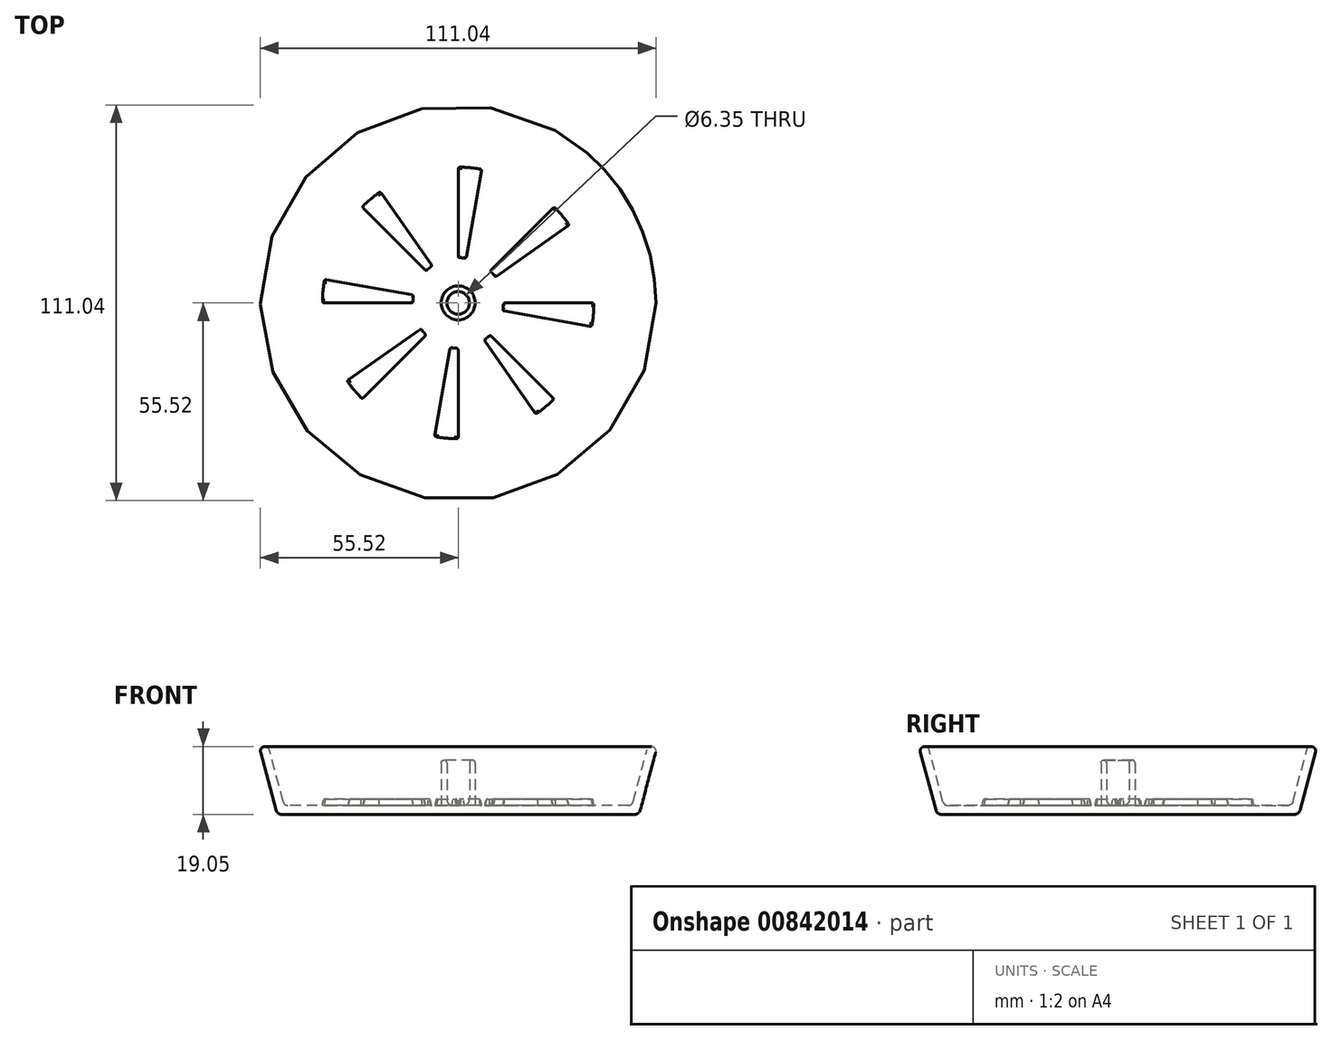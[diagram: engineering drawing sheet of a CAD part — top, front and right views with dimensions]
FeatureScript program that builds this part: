
annotation { "Feature Type Name" : "Feature", "Feature Type Description" : "" }
export const myFeature = defineFeature(function(context is Context, id is Id, definition is map)
    precondition{}
    {
        {
            var Q0;
            Q0=qCreatedBy(makeId("Top.planeOp"),FACE);
            var sketch = newSketch(context, id + "F0", { "sketchPlane" : qUnion([Q0])});
            skCircle(sketch, "E0.cCircle", {"center": v(0, 0) * mm, "radius": 38.1 * mm, "construction": true});
            skLineSegment(sketch, "E0.0", {"start": v(1.85, 47.06) * mm, "end": v(45.33, 12.78) * mm, "construction": true});
            skLineSegment(sketch, "E0.1", {"start": v(45.33, 12.78) * mm, "end": v(26.16, -39.16) * mm, "construction": true});
            skLineSegment(sketch, "E0.2", {"start": v(26.16, -39.16) * mm, "end": v(-29.16, -36.98) * mm, "construction": true});
            skLineSegment(sketch, "E0.3", {"start": v(-29.16, -36.98) * mm, "end": v(-44.18, 16.3) * mm, "construction": true});
            skLineSegment(sketch, "E0.4", {"start": v(-44.18, 16.3) * mm, "end": v(1.85, 47.06) * mm, "construction": true});
            skPoint(sketch, "E0.0.midPoint", {"position": v(23.59, 29.92) * mm});
            skCircle(sketch, "E1", {"center": v(0, 0) * mm, "radius": 50.8 * mm});
            skSolve(sketch);
        }
        {
            var Q0;
            Q0 = qSketchRegion(id + "F0", true);
            extrude(context, id + "F1", {"entities" : qUnion([Q0]), "depth" : 19.05 * mm, "offsetDistance" : 25.4 * mm, "hasDraft" : true, "draftAngle" : 15 * degree});
        }
        {
            var Q0;
            Q0=makeQuery(id+"F1.opExtrude","CAP_FACE",FACE,{"disambiguationData":[OSD([sQuery(id+"F0.wireOp",EDGE,"E1")])],"isStart":false});
            shell(context, id + "F2", {"entities" : qUnion([Q0]), "thickness" : 2.54 * mm});
        }
        {
            var Q0;
            Q0=makeQuery(id+"F1.opExtrude","CAP_FACE",FACE,{"disambiguationData":[OSD([sQuery(id+"F0.wireOp",EDGE,"E1")])],"isStart":false});
            var Q1;
            {var subQ0=sQuery(id+"F0.wireOp",EDGE,"E1");Q1=makeQuery(id+"F2.opShell","OFFSET_EDGE",EDGE,{"disambiguationData":[OSD([subQ0]),TDD([makeQuery(id+"F1.opExtrude","CAP_EDGE",EDGE,{"disambiguationData":[OSD([subQ0])],"isStart":true})])]});}
            fillet(context, id + "F3", {"entities" : qUnion([Q0, Q1]), "radius" : 1.27 * mm, "tangentPropagation" : true, "allowEdgeOverflow" : false});
        }
        {
            var Q0;
            {var subQ0=sQuery(id+"F0.wireOp",EDGE,"E1");Q0=makeQuery(id+"F2.opShell","OFFSET_FACE",FACE,{"disambiguationData":[OSD([subQ0]),TDD([makeQuery(id+"F1.opExtrude","CAP_FACE",FACE,{"disambiguationData":[OSD([subQ0])],"isStart":true})])]});}
            var sketch = newSketch(context, id + "F4", { "sketchPlane" : qUnion([Q0])});
            skCircle(sketch, "E2", {"center": v(0, 0) * mm, "radius": 4.76 * mm});
            skCircle(sketch, "E3", {"center": v(0, 0) * mm, "radius": 3.18 * mm});
            skSolve(sketch);
        }
        {
            var Q0;
            Q0=makeQuery(id+"F4.imprint","IMPRINT",FACE,{"disambiguationData":[TD([[makeQuery(id+"F4.imprint","IMPRINT",EDGE,{"derivedFrom":sQuery(id+"F4.wireOp",EDGE,"E2")}),1.0]])]});
            extrude(context, id + "F5", {"entities" : qUnion([Q0]), "operationType" : NewBodyOperationType.ADD, "depth" : 12.7 * mm, "offsetDistance" : 25.4 * mm});
        }
        {
            var Q0;
            Q0=makeQuery(id+"F1.opExtrude","CAP_FACE",FACE,{"disambiguationData":[OSD([sQuery(id+"F0.wireOp",EDGE,"E1")])],"isStart":true});
            var Q1;
            Q1=makeQuery(id+"F5.opExtrude","CAP_EDGE",EDGE,{"disambiguationData":[OSD([sQuery(id+"F4.wireOp",EDGE,"E2")])],"isStart":true});
            fillet(context, id + "F6", {"entities" : qUnion([Q0, Q1]), "radius" : 1.59 * mm, "tangentPropagation" : true, "allowEdgeOverflow" : false});
        }
        {
            var Q0;
            Q0=makeQuery(id+"F5.opExtrude","CAP_EDGE",EDGE,{"disambiguationData":[OSD([sQuery(id+"F4.wireOp",EDGE,"E3")])],"isStart":true});
            fillet(context, id + "F7", {"entities" : qUnion([Q0]), "radius" : 1.59 * mm, "tangentPropagation" : true, "allowEdgeOverflow" : false});
        }
        {
            var Q0;
            Q0=makeQuery(id+"F5.opExtrude","CAP_FACE",FACE,{"disambiguationData":[OSD([sQuery(id+"F4.wireOp",EDGE,"E2"),sQuery(id+"F4.wireOp",EDGE,"E3")])],"isStart":false});
            fillet(context, id + "F8", {"entities" : qUnion([Q0]), "radius" : 0.76 * mm, "tangentPropagation" : true, "allowEdgeOverflow" : false});
        }
        {
            var Q0;
            {var subQ0=sQuery(id+"F0.wireOp",EDGE,"E1");Q0=makeQuery(id+"F5.boolean.opBoolean","SPLIT",FACE,{"disambiguationData":[TD([makeQuery(id+"F5.opExtrude","SWEPT_FACE",FACE,{"disambiguationData":[OSD([sQuery(id+"F4.wireOp",EDGE,"E2")])]})])],"derivedFrom":makeQuery(id+"F2.opShell","OFFSET_FACE",FACE,{"disambiguationData":[OSD([subQ0]),TDD([makeQuery(id+"F1.opExtrude","CAP_FACE",FACE,{"disambiguationData":[OSD([subQ0])],"isStart":true})])]})});}
            var sketch = newSketch(context, id + "F9", { "sketchPlane" : qUnion([Q0])});
            skArc(sketch, "E4", {"start": v(2.2, 12.5) * mm, "mid": v(1.1, 12.65) * mm, "end": v(0, 12.7) * mm});
            skArc(sketch, "E5.0", {"start": v(6.62, 37.52) * mm, "mid": v(3.32, 37.96) * mm, "end": v(0, 38.1) * mm});
            skLineSegment(sketch, "E6", {"start": v(0, 38.1) * mm, "end": v(0, 12.7) * mm});
            skLineSegment(sketch, "E7.1.0", {"start": v(6.62, 37.52) * mm, "end": v(2.2, 12.5) * mm});
            skLineSegment(sketch, "E7.anchor1", {"start": v(0, 0) * mm, "end": v(0, 12.7) * mm, "construction": true});
            skLineSegment(sketch, "E7.anchor2", {"start": v(0, 0) * mm, "end": v(2.2, 12.5) * mm, "construction": true});
            skSolve(sketch);
        }
        {
            var Q0;
            Q0 = qSketchRegion(id + "F9", true);
            extrude(context, id + "F10", {"entities" : qUnion([Q0]), "operationType" : NewBodyOperationType.ADD, "depth" : 1.78 * mm, "offsetDistance" : 25.4 * mm, "hasDraft" : true, "draftAngle" : 10 * degree, "draftPullDirection" : true});
        }
        {
            var Q0;
            Q0=makeQuery(id+"F10.opExtrude","CAP_FACE",FACE,{"disambiguationData":[OSD([sQuery(id+"F9.wireOp",EDGE,"E4"),sQuery(id+"F9.wireOp",EDGE,"E5.0"),sQuery(id+"F9.wireOp",EDGE,"E6"),sQuery(id+"F9.wireOp",EDGE,"E7.1.0")])],"isStart":false});
            var Q1;
            Q1=makeQuery(id+"F10.opExtrude","SWEPT_EDGE",EDGE,{"disambiguationData":[OSD([sQuery(id+"F9.wireOp",EDGE,"E4"),sQuery(id+"F9.wireOp",EDGE,"E6")])]});
            var Q2;
            Q2=makeQuery(id+"F10.opExtrude","CAP_EDGE",EDGE,{"disambiguationData":[OSD([sQuery(id+"F9.wireOp",EDGE,"E6")])],"isStart":true});
            var Q3;
            Q3=makeQuery(id+"F10.opExtrude","SWEPT_EDGE",EDGE,{"disambiguationData":[OSD([sQuery(id+"F9.wireOp",EDGE,"E4"),sQuery(id+"F9.wireOp",EDGE,"E7.1.0")])]});
            var Q4;
            Q4=makeQuery(id+"F10.opExtrude","CAP_EDGE",EDGE,{"disambiguationData":[OSD([sQuery(id+"F9.wireOp",EDGE,"E5.0")])],"isStart":true});
            var Q5;
            Q5=makeQuery(id+"F10.opExtrude","SWEPT_EDGE",EDGE,{"disambiguationData":[OSD([sQuery(id+"F9.wireOp",EDGE,"E5.0"),sQuery(id+"F9.wireOp",EDGE,"E6")])]});
            var Q6;
            Q6=makeQuery(id+"F10.opExtrude","SWEPT_EDGE",EDGE,{"disambiguationData":[OSD([sQuery(id+"F9.wireOp",EDGE,"E5.0"),sQuery(id+"F9.wireOp",EDGE,"E7.1.0")])]});
            fillet(context, id + "F11", {"entities" : qUnion([Q0, Q1, Q2, Q3, Q4, Q5, Q6]), "radius" : 0.5 * mm, "tangentPropagation" : true, "allowEdgeOverflow" : false});
        }
        {
            var Q0;
            Q0=makeQuery(id+"F1.opExtrude","SWEPT_BODY",BODY,{"disambiguationData":[OSD([sQuery(id+"F0.wireOp",EDGE,"E1")])]});
            var Q1;
            {var subQ0=sQuery(id+"F0.wireOp",EDGE,"E1");Q1=makeQuery(id+"F3.opFillet","BLEND_EDGE",EDGE,{"blendedFrom":[makeQuery(id+"F1.opExtrude","CAP_EDGE",EDGE,{"disambiguationData":[OSD([subQ0])],"isStart":false}),makeQuery(id+"F1.opExtrude","SWEPT_FACE",FACE,{"disambiguationData":[OSD([subQ0])]})],"blendedInto":[makeQuery(id+"F1.opExtrude","SWEPT_FACE",FACE,{"disambiguationData":[OSD([subQ0])]})]});}
            circularPattern(context, id + "F12", {"operationType" : NewBodyOperationType.ADD, "entities" : qUnion([Q0]), "axis" : qUnion([Q1]), "angle" : 360 * degree, "instanceCount" : 8, "equalSpace" : true});
        }
    });
